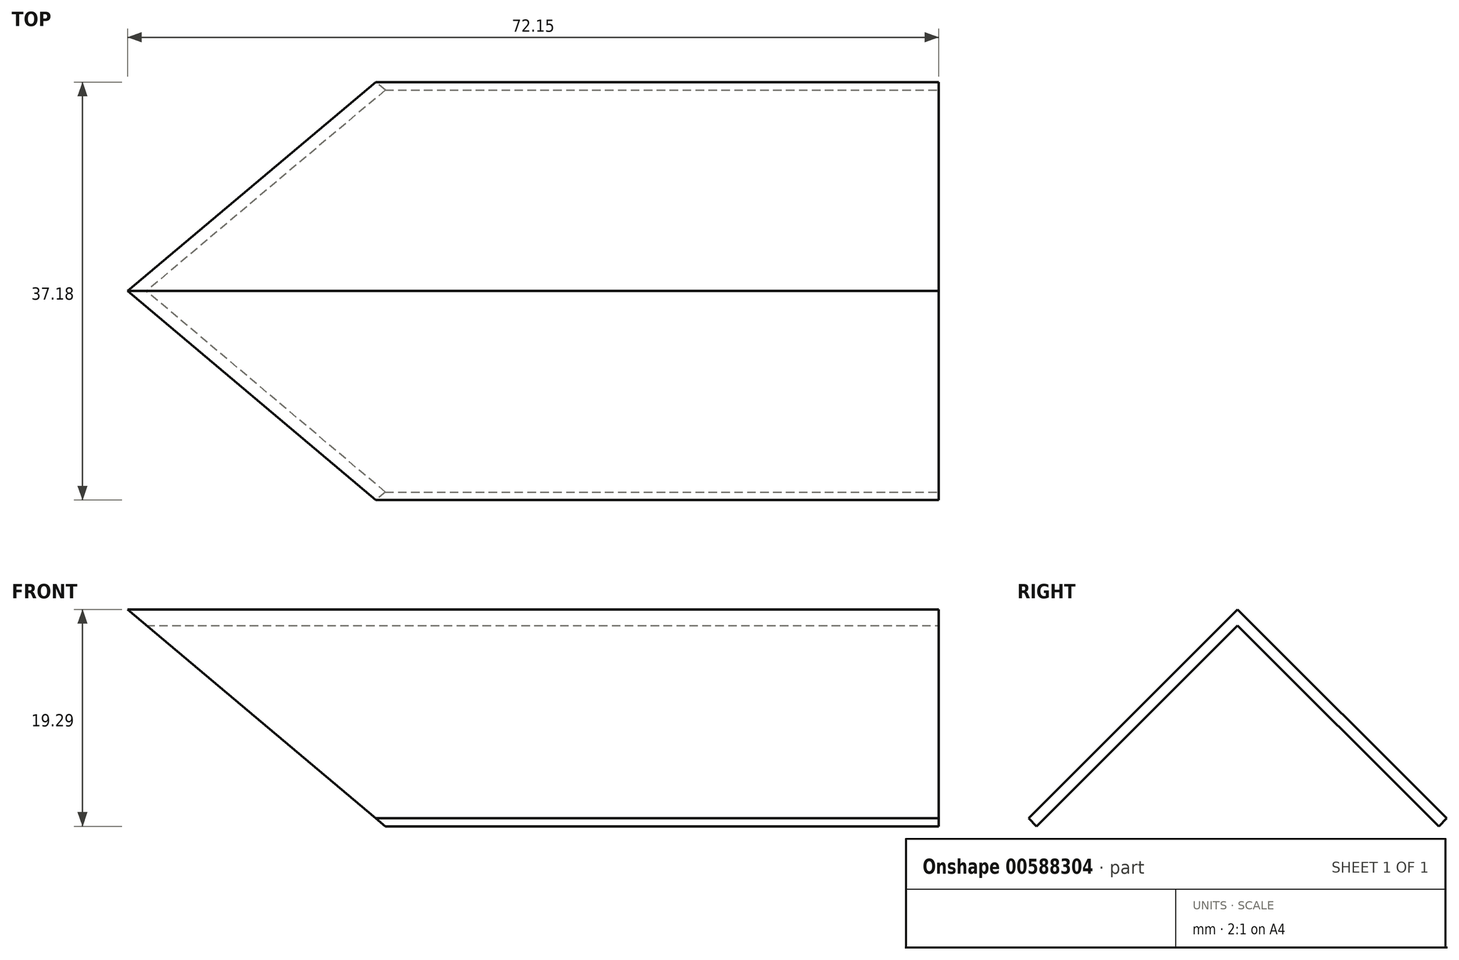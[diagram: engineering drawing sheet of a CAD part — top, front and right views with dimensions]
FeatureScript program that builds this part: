
annotation { "Feature Type Name" : "Feature", "Feature Type Description" : "" }
export const myFeature = defineFeature(function(context is Context, id is Id, definition is map)
    precondition{}
    {
        {
            var Q0;
            Q0=qCreatedBy(makeId("Front.planeOp"),FACE);
            var sketch = newSketch(context, id + "F0", { "sketchPlane" : qUnion([Q0])});
            skLineSegment(sketch, "E0", {"start": v(-97.77, 76.26) * mm, "end": v(-79.77, 42.96) * mm});
            skLineSegment(sketch, "E1", {"start": v(-127.77, 101.51) * mm, "end": v(-97.77, 76.26) * mm});
            skLineSegment(sketch, "E2", {"start": v(-127.77, 101.51) * mm, "end": v(-157.77, 76.26) * mm});
            skLineSegment(sketch, "E3", {"start": v(-175.77, 42.96) * mm, "end": v(-157.77, 76.26) * mm});
            skLineSegment(sketch, "E4", {"start": v(-175.77, 42.96) * mm, "end": v(-178.77, 42.96) * mm});
            skLineSegment(sketch, "E5", {"start": v(-79.77, 42.96) * mm, "end": v(-76.77, 42.96) * mm});
            skLineSegment(sketch, "E6.0", {"start": v(-96.98, 76.9) * mm, "end": v(-78.89, 43.44) * mm});
            skLineSegment(sketch, "E6.1", {"start": v(-127.77, 102.82) * mm, "end": v(-96.98, 76.9) * mm});
            skLineSegment(sketch, "E6.2", {"start": v(-127.77, 102.82) * mm, "end": v(-158.56, 76.9) * mm});
            skLineSegment(sketch, "E6.3", {"start": v(-177.84, 41.23) * mm, "end": v(-158.56, 76.9) * mm});
            skLineSegment(sketch, "E7", {"start": v(-175.77, 42.96) * mm, "end": v(-79.77, 42.96) * mm});
            skLineSegment(sketch, "E8", {"start": v(-78.89, 43.44) * mm, "end": v(-78.63, 42.96) * mm});
            skPoint(sketch, "E8.endSnap0", {"position": v(-78.27, 42.96) * mm});
            skPoint(sketch, "E9.orphan", {"position": v(-78.27, 42.3) * mm});
            skLineSegment(sketch, "E10", {"start": v(-175.77, 42.96) * mm, "end": v(-176.9, 42.96) * mm});
            skLineSegment(sketch, "E11", {"start": v(-127.77, 102.82) * mm, "end": v(-191.71, 102.82) * mm});
            skLineSegment(sketch, "E12", {"start": v(-127.77, 102.82) * mm, "end": v(-66.72, 102.82) * mm});
            skLineSegment(sketch, "E13", {"start": v(-176.9, 42.96) * mm, "end": v(-176.9, 107.35) * mm});
            skLineSegment(sketch, "E14", {"start": v(-78.63, 42.96) * mm, "end": v(-78.63, 110.13) * mm});
            skSolve(sketch);
        }
        {
            var Q0;
            Q0=makeQuery(id+"F0.imprint","IMPRINT",FACE,{"disambiguationData":[TD([[makeQuery(id+"F0.imprint","IMPRINT",EDGE,{"derivedFrom":sQuery(id+"F0.wireOp",EDGE,"E6.0")}),1.0]])]});
            var Q1;
            Q1=makeQuery(id+"F0.imprint","IMPRINT",FACE,{"disambiguationData":[TD([[makeQuery(id+"F0.imprint","IMPRINT",EDGE,{"derivedFrom":sQuery(id+"F0.wireOp",EDGE,"E0")}),-1.0]])]});
            var Q2;
            {var subQ5=sQuery(id+"F0.wireOp",EDGE,"E0");Q2=makeQuery(id+"F0.imprint","IMPRINT",FACE,{"disambiguationData":[TD([[makeQuery(id+"F0.imprint","IMPRINT",EDGE,{"derivedFrom":subQ5}),1.0]])]});}
            var Q3;
            {var subQ0=sQuery(id+"F0.wireOp",EDGE,"E6.2");Q3=makeQuery(id+"F0.imprint","IMPRINT",FACE,{"disambiguationData":[TD([[makeQuery(id+"F0.imprint","IMPRINT",EDGE,{"derivedFrom":subQ0}),-1.0]])]});}
            extrude(context, id + "F1", {"entities" : qUnion([Q0, Q1, Q2, Q3]), "oppositeDirection" : true, "depth" : 247.3 * mm, "offsetDistance" : 25 * mm});
        }
        {
            var Q0;
            Q0=makeQuery(id+"F1.opExtrude","SWEPT_FACE",FACE,{"disambiguationData":[OSD([sQuery(id+"F0.wireOp",EDGE,"E14")])]});
            var sketch = newSketch(context, id + "F2", { "sketchPlane" : qUnion([Q0])});
            skLineSegment(sketch, "E15.0", {"start": v(247.3, 102.82) * mm, "end": v(0, 102.82) * mm});
            skLineSegment(sketch, "E16.0", {"start": v(247.3, 42.96) * mm, "end": v(247.3, 102.82) * mm});
            skLineSegment(sketch, "E17.0", {"start": v(247.3, 42.96) * mm, "end": v(0, 42.96) * mm});
            skLineSegment(sketch, "E18.0", {"start": v(0, 42.96) * mm, "end": v(0, 110.13) * mm});
            skPoint(sketch, "E19.start.orphan", {"position": v(123.65, 102.82) * mm});
            skLineSegment(sketch, "E20", {"start": v(123.65, 102.82) * mm, "end": v(123.65, 42.96) * mm});
            skLineSegment(sketch, "E21", {"start": v(123.65, 102.82) * mm, "end": v(123.65, 84.6) * mm});
            skLineSegment(sketch, "E22", {"start": v(123.65, 102.82) * mm, "end": v(123.65, 82.82) * mm});
            skLineSegment(sketch, "E23", {"start": v(123.65, 82.82) * mm, "end": v(103.65, 82.82) * mm});
            skLineSegment(sketch, "E24", {"start": v(105.06, 84.23) * mm, "end": v(123.65, 102.82) * mm});
            skLineSegment(sketch, "E25", {"start": v(123.65, 82.82) * mm, "end": v(143.65, 82.82) * mm});
            skLineSegment(sketch, "E26", {"start": v(142.24, 84.23) * mm, "end": v(123.65, 102.82) * mm});
            skLineSegment(sketch, "E27", {"start": v(143.65, 82.82) * mm, "end": v(143.65, 42.96) * mm});
            skLineSegment(sketch, "E28", {"start": v(103.65, 82.82) * mm, "end": v(103.65, 42.96) * mm});
            skLineSegment(sketch, "E29.0", {"start": v(142.94, 82.11) * mm, "end": v(123.65, 101.4) * mm});
            skLineSegment(sketch, "E29.1", {"start": v(104.36, 82.11) * mm, "end": v(123.65, 101.4) * mm});
            skLineSegment(sketch, "E30", {"start": v(105.06, 84.23) * mm, "end": v(107.62, 81.68) * mm});
            skLineSegment(sketch, "E31", {"start": v(142.24, 84.23) * mm, "end": v(139.67, 81.66) * mm});
            skSolve(sketch);
        }
        {
            var Q0;
            Q0=makeQuery(id+"F0.imprint","IMPRINT",FACE,{"disambiguationData":[TD([[makeQuery(id+"F0.imprint","IMPRINT",EDGE,{"derivedFrom":sQuery(id+"F0.wireOp",EDGE,"E6.0")}),1.0]])]});
            extrude(context, id + "F3", {"entities" : qUnion([Q0]), "operationType" : NewBodyOperationType.REMOVE, "oppositeDirection" : true, "depth" : 300 * mm, "offsetDistance" : 25 * mm});
        }
        {
            var Q0;
            {var subQ0=sQuery(id+"F2.wireOp",EDGE,"E26");Q0=makeQuery(id+"F2.imprint","IMPRINT",FACE,{"disambiguationData":[TD([[makeQuery(id+"F2.imprint","IMPRINT",EDGE,{"derivedFrom":subQ0}),1.0]])]});}
            var Q1;
            {var subQ0=sQuery(id+"F2.wireOp",EDGE,"E24");Q1=makeQuery(id+"F2.imprint","IMPRINT",FACE,{"disambiguationData":[TD([[makeQuery(id+"F2.imprint","IMPRINT",EDGE,{"derivedFrom":subQ0}),-1.0]])]});}
            extrude(context, id + "F4", {"entities" : qUnion([Q0, Q1]), "operationType" : NewBodyOperationType.ADD, "oppositeDirection" : true, "depth" : 50 * mm, "offsetDistance" : 25 * mm});
        }
        {
            var Q0;
            {var subQ1=sQuery(id+"F2.wireOp",EDGE,"E22");var subQ3=makeQuery(id+"F2.imprint","IMPRINT",VERTEX,{"derivedFrom":subQ1});Q0=makeQuery(id+"F2.imprint","IMPRINT",FACE,{"disambiguationData":[TD([[makeQuery(id+"F2.imprint","IMPRINT",EDGE,{"disambiguationData":[TD([[subQ3,1.0]])],"derivedFrom":subQ1}),-1.0]])]});}
            var Q1;
            {var subQ1=sQuery(id+"F2.wireOp",EDGE,"E22");var subQ3=makeQuery(id+"F2.imprint","IMPRINT",VERTEX,{"derivedFrom":subQ1});Q1=makeQuery(id+"F2.imprint","IMPRINT",FACE,{"disambiguationData":[TD([[makeQuery(id+"F2.imprint","IMPRINT",EDGE,{"disambiguationData":[TD([[subQ3,1.0]])],"derivedFrom":subQ1}),1.0]])]});}
            var Q2;
            {var subQ1=sQuery(id+"F2.wireOp",EDGE,"E20");Q2=makeQuery(id+"F2.imprint","IMPRINT",FACE,{"disambiguationData":[TD([[makeQuery(id+"F2.imprint","IMPRINT",EDGE,{"derivedFrom":subQ1}),-1.0]])]});}
            var Q3;
            {var subQ3=sQuery(id+"F2.wireOp",EDGE,"E20");Q3=makeQuery(id+"F2.imprint","IMPRINT",FACE,{"disambiguationData":[TD([[makeQuery(id+"F2.imprint","IMPRINT",EDGE,{"derivedFrom":subQ3}),1.0]])]});}
            extrude(context, id + "F5", {"entities" : qUnion([Q0, Q1, Q2, Q3]), "operationType" : NewBodyOperationType.ADD, "oppositeDirection" : true, "depth" : 59.1 * mm, "offsetDistance" : 25 * mm});
        }
        {
            var Q0;
            {var subQ1=sQuery(id+"F2.wireOp",EDGE,"E20");Q0=makeQuery(id+"F2.imprint","IMPRINT",FACE,{"disambiguationData":[TD([[makeQuery(id+"F2.imprint","IMPRINT",EDGE,{"derivedFrom":subQ1}),-1.0]])]});}
            var Q1;
            {var subQ1=sQuery(id+"F2.wireOp",EDGE,"E22");var subQ3=makeQuery(id+"F2.imprint","IMPRINT",VERTEX,{"derivedFrom":subQ1});Q1=makeQuery(id+"F2.imprint","IMPRINT",FACE,{"disambiguationData":[TD([[makeQuery(id+"F2.imprint","IMPRINT",EDGE,{"disambiguationData":[TD([[subQ3,1.0]])],"derivedFrom":subQ1}),-1.0]])]});}
            var Q2;
            {var subQ1=sQuery(id+"F2.wireOp",EDGE,"E22");var subQ3=makeQuery(id+"F2.imprint","IMPRINT",VERTEX,{"derivedFrom":subQ1});Q2=makeQuery(id+"F2.imprint","IMPRINT",FACE,{"disambiguationData":[TD([[makeQuery(id+"F2.imprint","IMPRINT",EDGE,{"disambiguationData":[TD([[subQ3,1.0]])],"derivedFrom":subQ1}),1.0]])]});}
            var Q3;
            {var subQ3=sQuery(id+"F2.wireOp",EDGE,"E20");Q3=makeQuery(id+"F2.imprint","IMPRINT",FACE,{"disambiguationData":[TD([[makeQuery(id+"F2.imprint","IMPRINT",EDGE,{"derivedFrom":subQ3}),1.0]])]});}
            extrude(context, id + "F6", {"entities" : qUnion([Q0, Q1, Q2, Q3]), "operationType" : NewBodyOperationType.REMOVE, "oppositeDirection" : true, "depth" : 300 * mm, "offsetDistance" : 25 * mm});
        }
        {
            var Q0;
            {var subQ0=sQuery(id+"F0.wireOp",EDGE,"E6.2");Q0=makeQuery(id+"F0.imprint","IMPRINT",FACE,{"disambiguationData":[TD([[makeQuery(id+"F0.imprint","IMPRINT",EDGE,{"derivedFrom":subQ0}),-1.0]])]});}
            var Q1;
            {var subQ5=sQuery(id+"F0.wireOp",EDGE,"E0");Q1=makeQuery(id+"F0.imprint","IMPRINT",FACE,{"disambiguationData":[TD([[makeQuery(id+"F0.imprint","IMPRINT",EDGE,{"derivedFrom":subQ5}),1.0]])]});}
            var Q2;
            Q2=makeQuery(id+"F0.imprint","IMPRINT",FACE,{"disambiguationData":[TD([[makeQuery(id+"F0.imprint","IMPRINT",EDGE,{"derivedFrom":sQuery(id+"F0.wireOp",EDGE,"E0")}),-1.0]])]});
            extrude(context, id + "F7", {"entities" : qUnion([Q0, Q1, Q2]), "operationType" : NewBodyOperationType.REMOVE, "oppositeDirection" : true, "depth" : 300 * mm, "offsetDistance" : 25 * mm});
        }
        {
            var Q0;
            {var subQ0=sQuery(id+"F2.wireOp",EDGE,"E24");Q0=makeQuery(id+"F2.imprint","IMPRINT",FACE,{"disambiguationData":[TD([[makeQuery(id+"F2.imprint","IMPRINT",EDGE,{"derivedFrom":subQ0}),-1.0]])]});}
            var Q1;
            {var subQ0=sQuery(id+"F2.wireOp",EDGE,"E26");Q1=makeQuery(id+"F2.imprint","IMPRINT",FACE,{"disambiguationData":[TD([[makeQuery(id+"F2.imprint","IMPRINT",EDGE,{"derivedFrom":subQ0}),1.0]])]});}
            extrude(context, id + "F8", {"entities" : qUnion([Q0, Q1]), "operationType" : NewBodyOperationType.ADD, "depth" : 17.1 * mm, "offsetDistance" : 25 * mm});
        }
        {
            var Q0;
            Q0=makeQuery(id+"F8.opExtrude","CAP_FACE",FACE,{"disambiguationData":[OSD([sQuery(id+"F2.wireOp",EDGE,"E24"),sQuery(id+"F2.wireOp",EDGE,"E26"),sQuery(id+"F2.wireOp",EDGE,"E29.0"),sQuery(id+"F2.wireOp",EDGE,"E29.1"),sQuery(id+"F2.wireOp",EDGE,"E30"),sQuery(id+"F2.wireOp",EDGE,"E31")])],"isStart":false});
            extrude(context, id + "F9", {"entities" : qUnion([Q0]), "operationType" : NewBodyOperationType.ADD, "depth" : 1.9 * mm, "offsetDistance" : 25 * mm});
        }
        {
            var Q0;
            Q0=makeQuery(id+"F9.opExtrude","CAP_FACE",FACE,{"disambiguationData":[OSD([sQuery(id+"F2.wireOp",EDGE,"E24"),sQuery(id+"F2.wireOp",EDGE,"E26"),sQuery(id+"F2.wireOp",EDGE,"E29.0"),sQuery(id+"F2.wireOp",EDGE,"E29.1"),sQuery(id+"F2.wireOp",EDGE,"E30"),sQuery(id+"F2.wireOp",EDGE,"E31")])],"isStart":false});
            extrude(context, id + "F10", {"entities" : qUnion([Q0]), "operationType" : NewBodyOperationType.ADD, "depth" : 1 * mm, "offsetDistance" : 25 * mm});
        }
        {
            var Q0;
            Q0=makeQuery(id+"F10.opExtrude","CAP_FACE",FACE,{"disambiguationData":[OSD([sQuery(id+"F2.wireOp",EDGE,"E24"),sQuery(id+"F2.wireOp",EDGE,"E26"),sQuery(id+"F2.wireOp",EDGE,"E29.0"),sQuery(id+"F2.wireOp",EDGE,"E29.1"),sQuery(id+"F2.wireOp",EDGE,"E30"),sQuery(id+"F2.wireOp",EDGE,"E31")])],"isStart":false});
            extrude(context, id + "F11", {"entities" : qUnion([Q0]), "operationType" : NewBodyOperationType.ADD, "depth" : 3 * mm, "offsetDistance" : 25 * mm});
        }
    });
